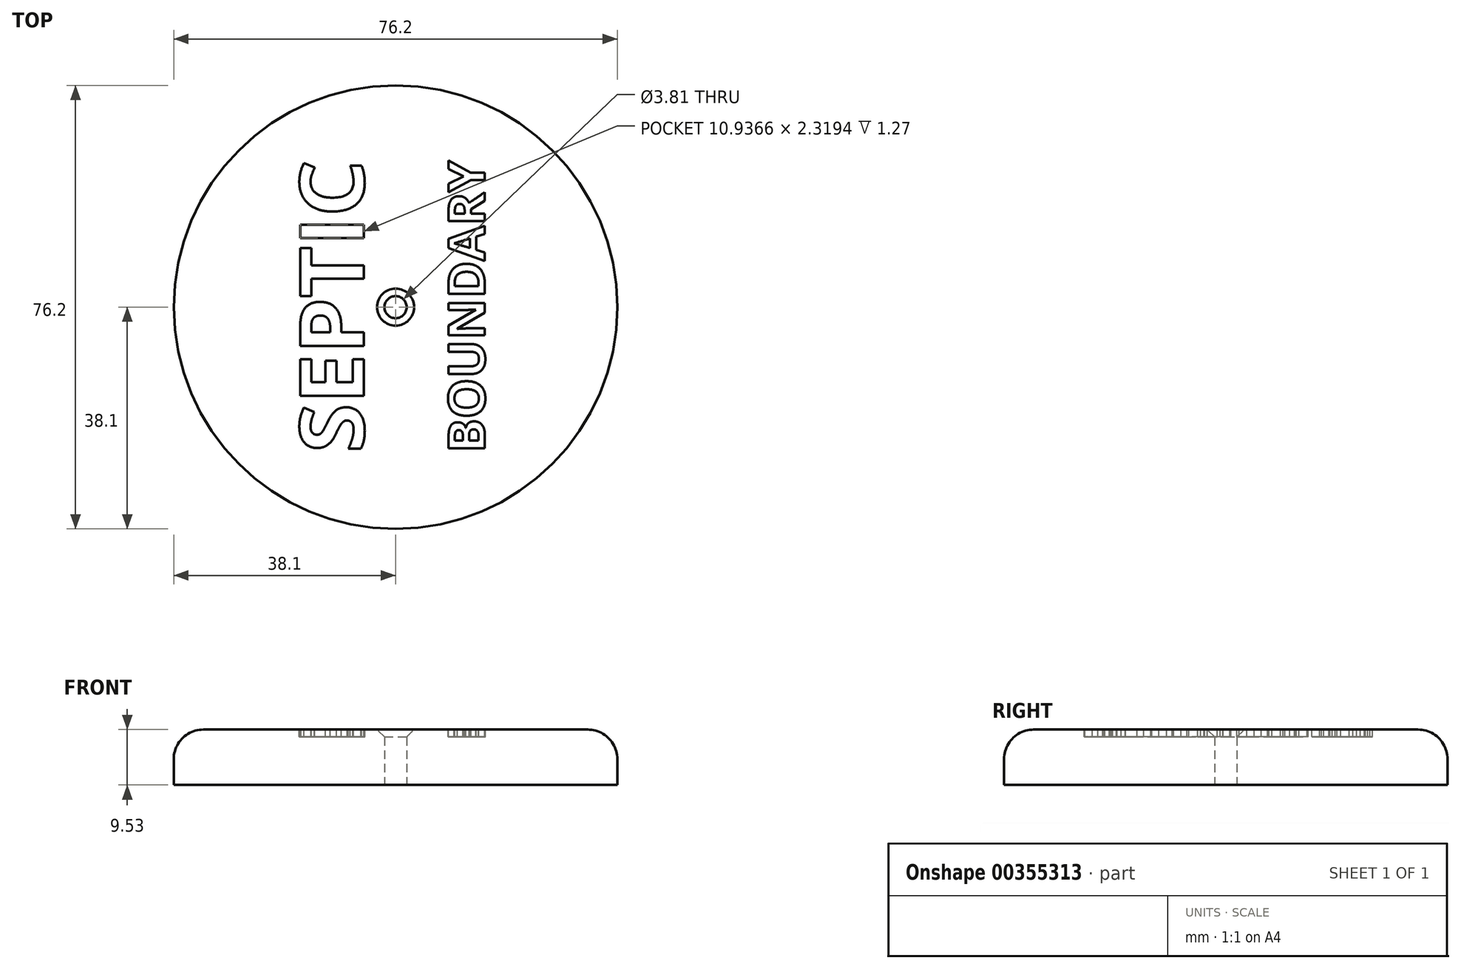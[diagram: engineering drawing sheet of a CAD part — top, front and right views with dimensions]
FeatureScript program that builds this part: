
annotation { "Feature Type Name" : "Feature", "Feature Type Description" : "" }
export const myFeature = defineFeature(function(context is Context, id is Id, definition is map)
    precondition{}
    {
        {
            var Q0;
            Q0=qCreatedBy(makeId("Top.planeOp"),FACE);
            var sketch = newSketch(context, id + "F0", { "sketchPlane" : qUnion([Q0])});
            skCircle(sketch, "E0", {"center": v(0, 0) * mm, "radius": 38.1 * mm});
            skSolve(sketch);
        }
        {
            var Q0;
            Q0=makeQuery(id+"F0.imprint","IMPRINT",FACE,{"disambiguationData":[TD([[makeQuery(id+"F0.imprint","IMPRINT",EDGE,{"derivedFrom":sQuery(id+"F0.wireOp",EDGE,"E0")}),1.0]])]});
            extrude(context, id + "F1", {"entities" : qUnion([Q0]), "depth" : 9.52 * mm});
        }
        {
            var Q0;
            Q0=makeQuery(id+"F1.opExtrude","CAP_FACE",FACE,{"disambiguationData":[OSD([sQuery(id+"F0.wireOp",EDGE,"E0")])],"isStart":true});
            var sketch = newSketch(context, id + "F2", { "sketchPlane" : qUnion([Q0])});
            skCircle(sketch, "E1", {"center": v(0, 0) * mm, "radius": 1.9 * mm});
            skSolve(sketch);
        }
        {
            var Q0;
            Q0=makeQuery(id+"F1.opExtrude","CAP_EDGE",EDGE,{"disambiguationData":[OSD([sQuery(id+"F0.wireOp",EDGE,"E0")])],"isStart":false});
            fillet(context, id + "F3", {"entities" : qUnion([Q0]), "radius" : 5.08 * mm, "tangentPropagation" : true, "allowEdgeOverflow" : false});
        }
        {
            var Q0;
            Q0=makeQuery(id+"F1.opExtrude","CAP_FACE",FACE,{"disambiguationData":[OSD([sQuery(id+"F0.wireOp",EDGE,"E0")])],"isStart":false});
            var sketch = newSketch(context, id + "F4", { "sketchPlane" : qUnion([Q0])});
            skText(sketch, "E2", { "text": "SEPTIC", "fontName": "OpenSans-Bold.ttf"});
            skText(sketch, "E3", { "text": "BOUNDARY", "fontName": "OpenSans-Bold.ttf"});
            const initialGuessF4  = {"E2": [-0.00544, -0.02504, 0, 1, 0.01103], "E3": [0.01534, -0.02504, 0, 1, 0.00629]};
            skSetInitialGuess(sketch, initialGuessF4);
            skSolve(sketch);
        }
        {
            var Q0;
            Q0 = qSketchRegion(id + "F4", true);
            extrude(context, id + "F5", {"entities" : qUnion([Q0]), "operationType" : NewBodyOperationType.REMOVE, "oppositeDirection" : true, "depth" : 1.27 * mm});
        }
        {
            var Q0;
            Q0 = qSketchRegion(id + "F2", true);
            extrude(context, id + "F6", {"entities" : qUnion([Q0]), "operationType" : NewBodyOperationType.REMOVE, "oppositeDirection" : true, "depth" : 25.4 * mm});
        }
        {
            var Q0;
            {var subQ0=sQuery(id+"F0.wireOp",EDGE,"E0");Q0=makeQuery(id+"F6.boolean.opBoolean","INTERSECT",EDGE,{"derivedFrom":[makeQuery(id+"F5.boolean.opBoolean","SPLIT",FACE,{"disambiguationData":[TD([makeQuery(id+"F3.opFillet","BLEND_FACE",FACE,{"disambiguationData":[OSD([subQ0])]})])],"derivedFrom":makeQuery(id+"F1.opExtrude","CAP_FACE",FACE,{"disambiguationData":[OSD([subQ0])],"isStart":false})}),makeQuery(id+"F6.opExtrude","SWEPT_FACE",FACE,{"disambiguationData":[OSD([sQuery(id+"F2.wireOp",EDGE,"E1")])]})]});}
            chamfer(context, id + "F7", {"entities" : qUnion([Q0]), "width" : 1.27 * mm, "tangentPropagation" : true});
        }
    });
